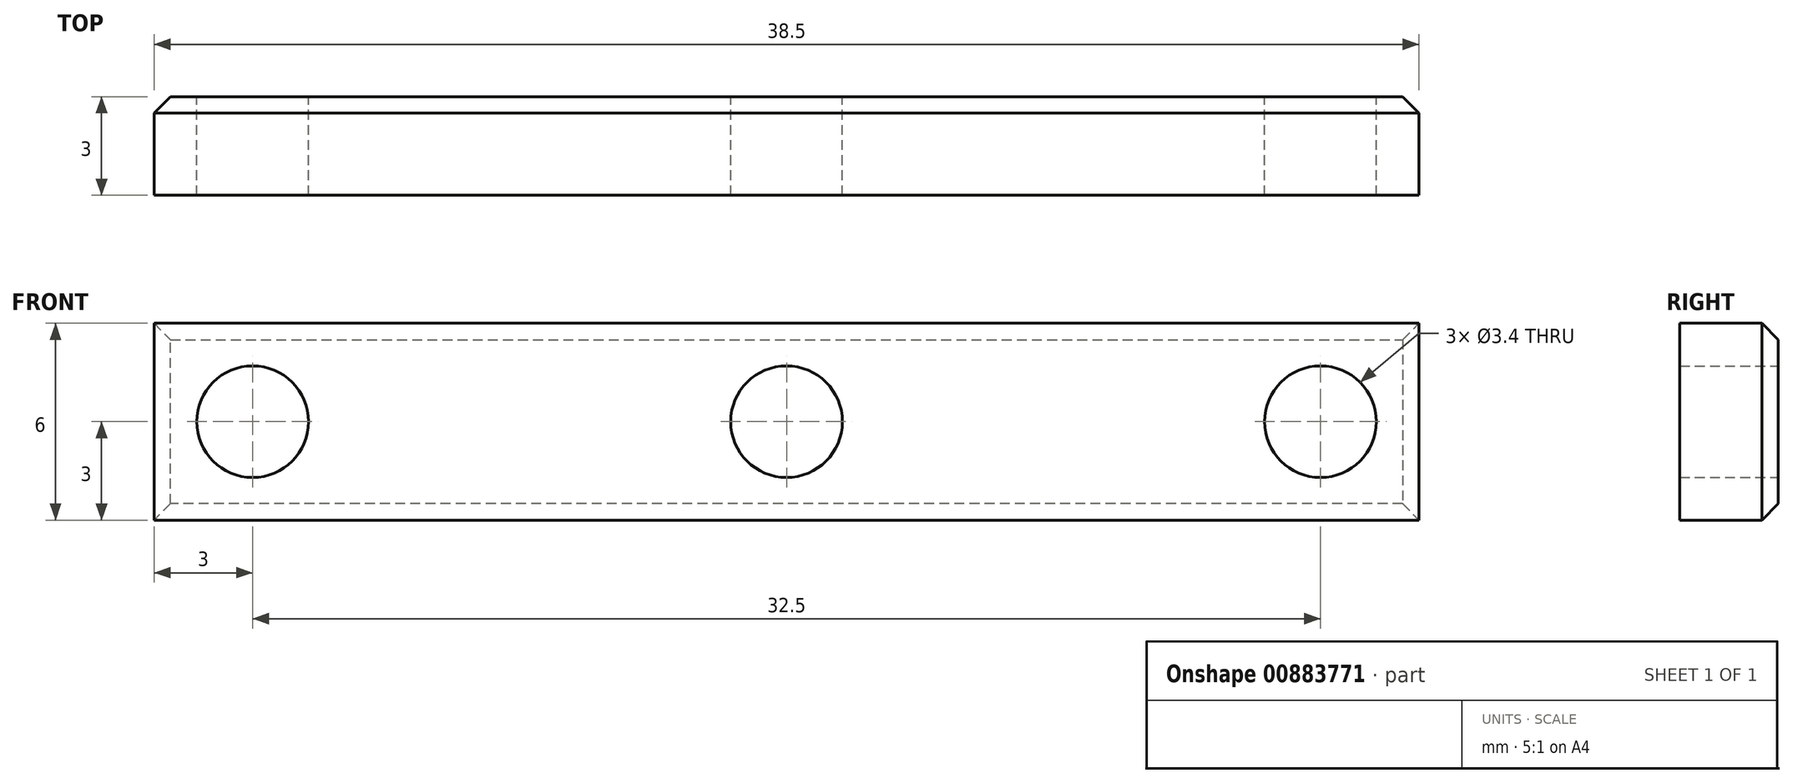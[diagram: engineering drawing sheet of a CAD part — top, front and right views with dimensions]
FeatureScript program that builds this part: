
annotation { "Feature Type Name" : "Feature", "Feature Type Description" : "" }
export const myFeature = defineFeature(function(context is Context, id is Id, definition is map)
    precondition{}
    {
        {
            var Q0;
            Q0=qCreatedBy(makeId("Front.planeOp"),FACE);
            var sketch = newSketch(context, id + "F0", { "sketchPlane" : qUnion([Q0])});
            skLineSegment(sketch, "E0", {"start": v(-19.25, 3) * mm, "end": v(-19.25, -3) * mm});
            skLineSegment(sketch, "E1", {"start": v(-19.25, -3) * mm, "end": v(19.25, -3) * mm});
            skLineSegment(sketch, "E2", {"start": v(19.25, -3) * mm, "end": v(19.25, 3) * mm});
            skLineSegment(sketch, "E3", {"start": v(19.25, 3) * mm, "end": v(-19.25, 3) * mm});
            skCircle(sketch, "E4", {"center": v(-16.25, 0) * mm, "radius": 1.7 * mm});
            skCircle(sketch, "E5", {"center": v(0, 0) * mm, "radius": 1.7 * mm});
            skCircle(sketch, "E6", {"center": v(16.25, 0) * mm, "radius": 1.7 * mm});
            skSolve(sketch);
        }
        {
            var Q0;
            Q0=makeQuery(id+"F0.imprint","IMPRINT",FACE,{"disambiguationData":[TD([[makeQuery(id+"F0.imprint","IMPRINT",EDGE,{"derivedFrom":sQuery(id+"F0.wireOp",EDGE,"E0")}),1.0]])]});
            extrude(context, id + "F1", {"entities" : qUnion([Q0]), "depth" : 3 * mm, "offsetDistance" : 25 * mm});
        }
        {
            var Q0;
            Q0=makeQuery(id+"F1.opExtrude","CAP_EDGE",EDGE,{"disambiguationData":[OSD([sQuery(id+"F0.wireOp",EDGE,"E1")])],"isStart":true});
            var Q1;
            Q1=makeQuery(id+"F1.opExtrude","CAP_EDGE",EDGE,{"disambiguationData":[OSD([sQuery(id+"F0.wireOp",EDGE,"E2")])],"isStart":true});
            var Q2;
            Q2=makeQuery(id+"F1.opExtrude","CAP_EDGE",EDGE,{"disambiguationData":[OSD([sQuery(id+"F0.wireOp",EDGE,"E3")])],"isStart":true});
            var Q3;
            Q3=makeQuery(id+"F1.opExtrude","CAP_EDGE",EDGE,{"disambiguationData":[OSD([sQuery(id+"F0.wireOp",EDGE,"E0")])],"isStart":true});
            chamfer(context, id + "F2", {"entities" : qUnion([Q0, Q1, Q2, Q3]), "width" : 0.5 * mm, "tangentPropagation" : true});
        }
    });
